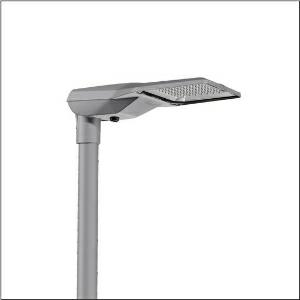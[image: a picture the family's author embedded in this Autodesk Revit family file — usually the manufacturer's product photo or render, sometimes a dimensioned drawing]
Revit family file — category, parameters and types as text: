
# Revit family: streetlight_sl_21_midi___st1_0ab_5xe3m33r08mb_c7ee
name_source: partatom
category: Lighting Fixtures
units: mm (PartAtom-declared; Revit-internal decimal feet)

## family parameters
Cut with Voids When Loaded = No
Host = Face
Light Source = No
Part Type = Normal
Room Calculation Point = No
Round Connector Dimension = Use Diameter
Shared = No

## types (1)
- --- (1 x LED, 16080 lm, 136 W, 3000K)
    Apparent Load = 136 VA
    CIE Flux Codes = 38 73 97 100 100
    Color Rendering = 70
    Color Temperature = 3000K
    Default Elevation = 1800 mm
    Description = Streetlight SL 21 midi, mast luminaire, primary light control with lens, of PMMA, primary optical cover: cover, of toughened safety glass, transparent, light distribution: ST1.0aB, light emission: direct distribution, primary light characteristic: asymmetric, installation type: side-entry, post-top, LED, High Power LED, rated luminous flux: 16.080lm, luminous efficacy: 118lm/W, light colour: 730, colour temperature: 3000K, control gear: D4i, control: flexible luminous flux parameterisation, time-dependent luminous flux control, constant luminous flux control, overheat protection, pre-setting: logarithmic dimming characteristic, mains connection: 230..240V, AC, 50/60Hz, start of lifetime: 136W, end of service life: 142W, reduction: 61W, luminaire housing, of diecast aluminium, powder-coated, Siteco® metallic grey (DB 702S), corrosivity category C5 mid according to DIN EN ISO 12944, please order mast flange separately, inclination adjustable: 0°, 5°, 10°, 15°, sealing non-destructively replaceable, multi-level sealing system, length: 644mm, width: 335mm, height: 110mm, mast flange for spigot size: 42mm (side-entry): 5XC10008XM4, 60/48mm (side-entry/post-top): 5XC10108XM2, 76/60mm (side-entry/post-top): 5XC10108XM1, mounting height: 4..8m, Smart Interface below, protection rating (complete): IP66, insulation class (complete): insulation class II (safety insulation), certification: CE, ENEC, ENEC+, VDE, impact resistance: IK10, permissible operating ambient temperature for outdoor applications: -40..+50°C, standard-compliant lighting for roads and squares, packaging unit: 1 piece

Light Distribution: ST1.0aB
    Height = 111 mm
    Lamp = 1 x LED
    Lamp Light Flux = 16080 lm
    Lamp Power = 136 W
    Lamp count = 1
    Length = 644 mm
    Luminous efficacy = 118 lm/W
    Manufacturer = Siteco
    ModVariant = No
    Model = 5XE3M33R08MB
    Number of Poles = 1
    OnlyDefault = Yes
    Power Factor = 1
    Product Name = Streetlight SL 21 midi | ST1.0aB
    Product group = mast luminaire | pylon top
    ProductGroupID = 6100
    Protection Class = Protection class II
    Protection Degree = IP 66
    RLX_Detail_Level = 1
    RLX_Emergency_Light_Flux = 0 lm
    RLX_Emergency_Type = 0
    RLX_Emergency_Type_DB = No
    RlxData = <blob elided: 26985 chars, md5=154f4672>
    Socket = socket
    Standby Power = 0 W
    System Light Flux = 16081 lm
    System Power = 136 W
    Type Comments = factory setting: luminous flux: 100 % | dim-lin: 254 | 695 mA
    Type Image = l_1004300.jpg
    URL = http://relux.com
    VarID = @adj_204259
    Voltage = 0 V
    Weight = 0.00 kg
    Width = 336 mm

## geometry (parser evidence)
native form markers: Blend x4, Sweep x11
no freeform markers — native parametric forms only
